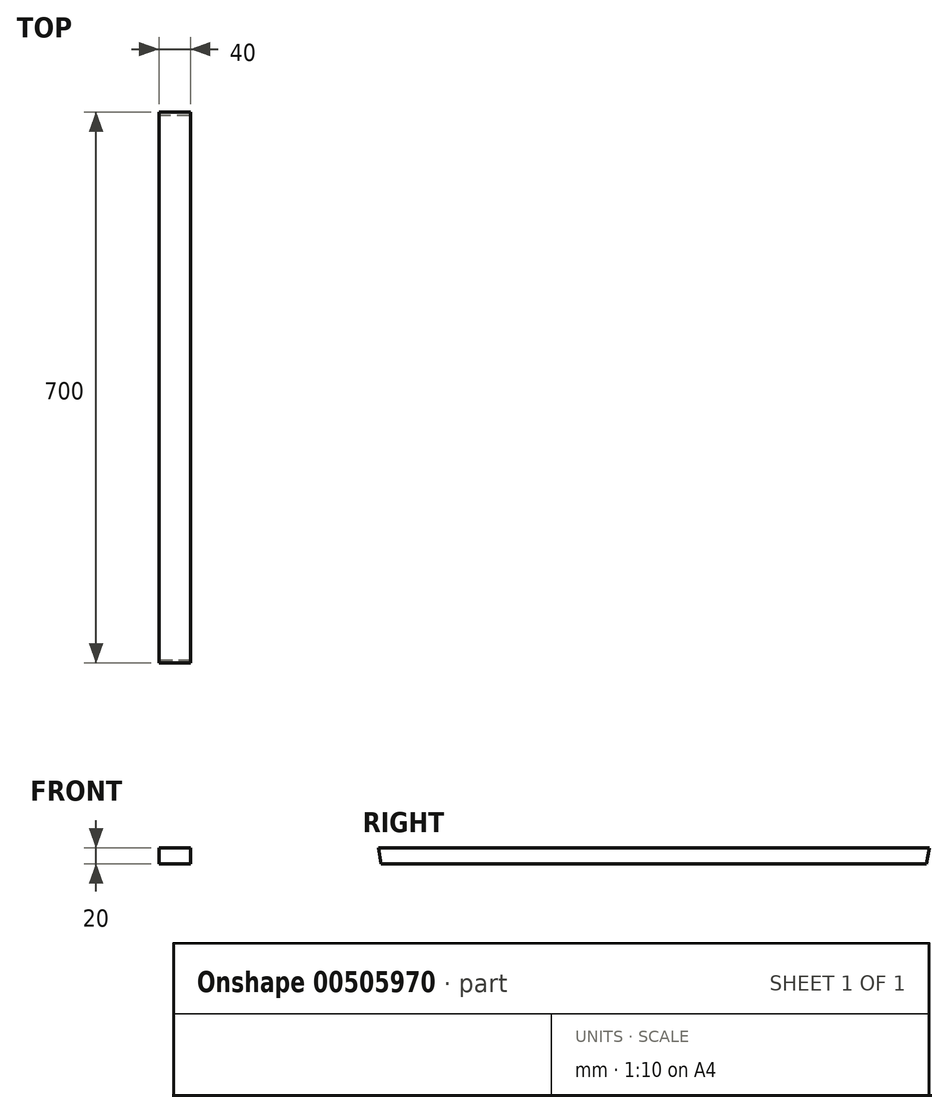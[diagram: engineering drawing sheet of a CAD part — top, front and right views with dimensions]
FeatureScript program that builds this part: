
annotation { "Feature Type Name" : "Feature", "Feature Type Description" : "" }
export const myFeature = defineFeature(function(context is Context, id is Id, definition is map)
    precondition{}
    {
        {
            var Q0;
            Q0=qCreatedBy(makeId("Front.planeOp"),FACE);
            var sketch = newSketch(context, id + "F0", { "sketchPlane" : qUnion([Q0])});
            skLineSegment(sketch, "E0.bottom", {"start": v(0, 0) * mm, "end": v(40, 0) * mm});
            skLineSegment(sketch, "E0.top", {"start": v(0, 20) * mm, "end": v(40, 20) * mm});
            skLineSegment(sketch, "E0.left", {"start": v(0, 0) * mm, "end": v(0, 20) * mm});
            skLineSegment(sketch, "E0.right", {"start": v(40, 0) * mm, "end": v(40, 20) * mm});
            skSolve(sketch);
        }
        {
            var Q0;
            Q0 = qSketchRegion(id + "F0", true);
            extrude(context, id + "F1", {"entities" : qUnion([Q0]), "depth" : 700 * mm, "offsetDistance" : 25 * mm});
        }
        {
            var Q0;
            Q0=makeQuery(id+"F1.opExtrude","CAP_EDGE",EDGE,{"disambiguationData":[OSD([sQuery(id+"F0.wireOp",EDGE,"E0.bottom")])],"isStart":false});
            chamfer(context, id + "F2", {"entities" : qUnion([Q0]), "chamferType" : ChamferType.OFFSET_ANGLE, "width" : 20 * mm, "oppositeDirection" : false, "angle" : 10 * degree, "tangentPropagation" : true});
        }
        {
            var Q0;
            Q0=makeQuery(id+"F1.opExtrude","CAP_EDGE",EDGE,{"disambiguationData":[OSD([sQuery(id+"F0.wireOp",EDGE,"E0.bottom")])],"isStart":true});
            chamfer(context, id + "F3", {"entities" : qUnion([Q0]), "chamferType" : ChamferType.OFFSET_ANGLE, "width" : 20 * mm, "oppositeDirection" : true, "angle" : 10 * degree, "tangentPropagation" : true});
        }
    });
